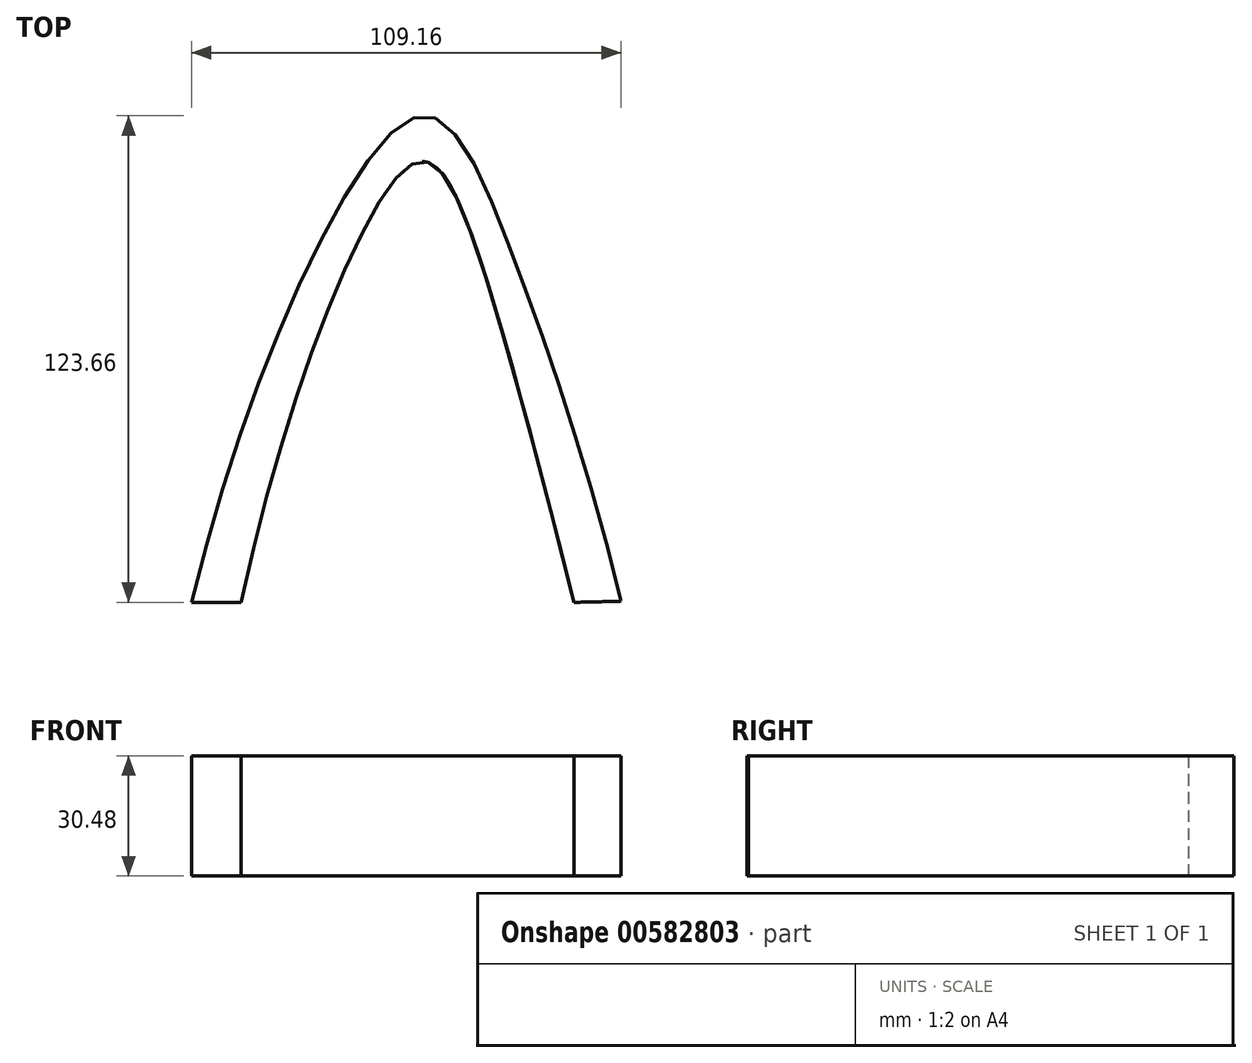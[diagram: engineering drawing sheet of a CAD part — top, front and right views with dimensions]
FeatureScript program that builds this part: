
annotation { "Feature Type Name" : "Feature", "Feature Type Description" : "" }
export const myFeature = defineFeature(function(context is Context, id is Id, definition is map)
    precondition{}
    {
        {
            var Q0;
            Q0=qCreatedBy(makeId("Top.planeOp"),FACE);
            var sketch = newSketch(context, id + "F0", { "sketchPlane" : qUnion([Q0])});
            skFitSpline(sketch, "E0", {"points": [v(-81.06, -54) * mm, v(-47.68, 38.95) * mm, v(-21.2, 69.63) * mm, v(0, 35.64) * mm, v(28.1, -53.7) * mm], "startDerivative": vector(83.33, 339.75) * mm, "endDerivative": vector(85.5, -346.56) * mm});
            skFitSpline(sketch, "E1", {"points": [v(-68.43, -54) * mm, v(-40.76, 33.54) * mm, v(-22.94, 58.08) * mm, v(-6.8, 30.13) * mm, v(16.07, -54) * mm, v(15.8, -54) * mm], "startDerivative": vector(68.97, 323.61) * mm, "endDerivative": vector(-48.1, 0) * mm});
            skFitSpline(sketch, "E2", {"points": [v(-81.06, -54) * mm, v(-68.43, -54) * mm], "startDerivative": vector(12.63, 0) * mm, "endDerivative": vector(12.63, 0) * mm});
            skFitSpline(sketch, "E3", {"points": [v(16.07, -54) * mm, v(28.1, -53.7) * mm], "startDerivative": vector(10.55, 0.3) * mm, "endDerivative": vector(10.55, 0.3) * mm});
            skSolve(sketch);
        }
        {
            var Q0;
            Q0=makeQuery(id+"F0.imprint","IMPRINT",FACE,{"disambiguationData":[TD([[makeQuery(id+"F0.imprint","IMPRINT",EDGE,{"derivedFrom":sQuery(id+"F0.wireOp",EDGE,"E0")}),-1.0]])]});
            extrude(context, id + "F1", {"entities" : qUnion([Q0]), "endBound" : BoundingType.SYMMETRIC, "depth" : 30.48 * mm, "offsetDistance" : 30.48 * mm});
        }
    });
